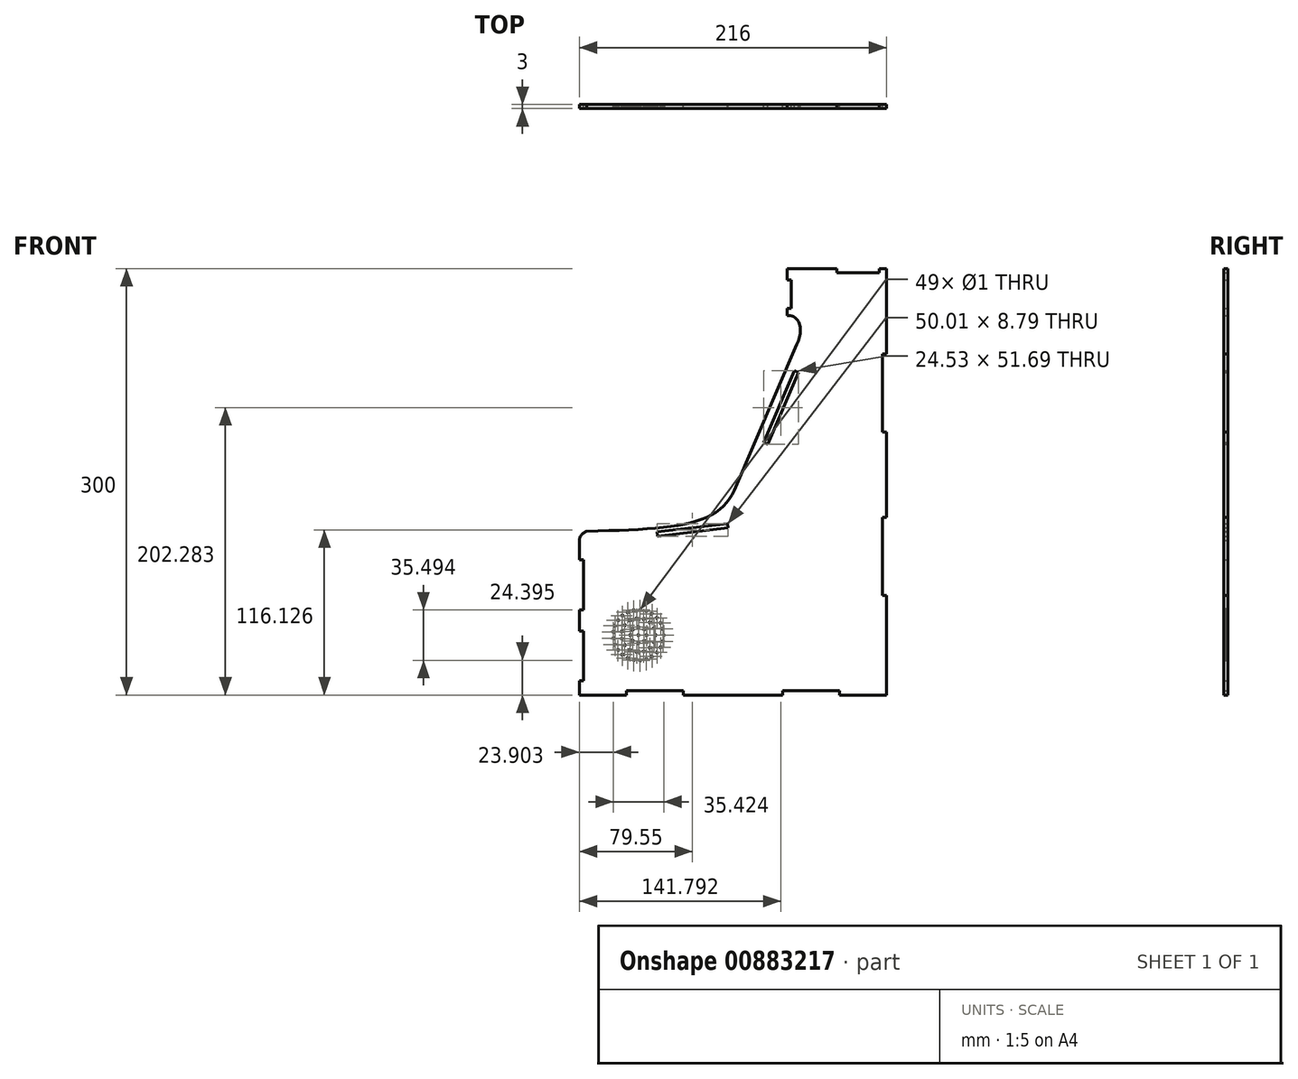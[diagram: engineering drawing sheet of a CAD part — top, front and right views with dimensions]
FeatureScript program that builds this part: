
annotation { "Feature Type Name" : "Feature", "Feature Type Description" : "" }
export const myFeature = defineFeature(function(context is Context, id is Id, definition is map)
    precondition{}
    {
        {
            var Q0;
            Q0=qCreatedBy(makeId("Front.planeOp"),FACE);
            var sketch = newSketch(context, id + "F0", { "sketchPlane" : qUnion([Q0])});
            skLineSegment(sketch, "E0.bottom", {"start": v(0, 0) * mm, "end": v(216, 0) * mm});
            skLineSegment(sketch, "E0.left", {"start": v(0, 0) * mm, "end": v(0, 115) * mm});
            skLineSegment(sketch, "E0.right", {"start": v(216, 0) * mm, "end": v(216, 300) * mm});
            skLineSegment(sketch, "E1", {"start": v(216, 300) * mm, "end": v(176, 300) * mm});
            skLineSegment(sketch, "E2", {"start": v(143, 0) * mm, "end": v(143, 3) * mm});
            skLineSegment(sketch, "E3", {"start": v(143, 3) * mm, "end": v(183, 3) * mm});
            skLineSegment(sketch, "E4", {"start": v(183, 3) * mm, "end": v(183, 0) * mm});
            skLineSegment(sketch, "E5", {"start": v(0, 45) * mm, "end": v(3, 45) * mm});
            skLineSegment(sketch, "E6", {"start": v(3, 45) * mm, "end": v(3, 10) * mm});
            skLineSegment(sketch, "E7", {"start": v(3, 10) * mm, "end": v(0, 10) * mm});
            skLineSegment(sketch, "E8", {"start": v(216, 125) * mm, "end": v(213, 125) * mm});
            skLineSegment(sketch, "E9", {"start": v(213, 125) * mm, "end": v(213, 70) * mm});
            skLineSegment(sketch, "E10", {"start": v(213, 70) * mm, "end": v(216, 70) * mm});
            skLineSegment(sketch, "E11", {"start": v(176, 300) * mm, "end": v(108.8, 144.17) * mm});
            skLineSegment(sketch, "E12", {"start": v(181, 300) * mm, "end": v(181, 297) * mm});
            skLineSegment(sketch, "E13", {"start": v(181, 297) * mm, "end": v(211, 297) * mm});
            skLineSegment(sketch, "E14", {"start": v(211, 297) * mm, "end": v(211, 300) * mm});
            skLineSegment(sketch, "E15", {"start": v(54.54, 114.7) * mm, "end": v(54.9, 111.73) * mm});
            skLineSegment(sketch, "E16", {"start": v(54.9, 111.73) * mm, "end": v(104.55, 117.54) * mm});
            skLineSegment(sketch, "E17", {"start": v(104.55, 117.54) * mm, "end": v(104.2, 120.52) * mm});
            skLineSegment(sketch, "E18", {"start": v(54.54, 114.7) * mm, "end": v(104.2, 120.52) * mm});
            skLineSegment(sketch, "E19", {"start": v(181, 297) * mm, "end": v(130.46, 179.8) * mm, "construction": true});
            skLineSegment(sketch, "E20", {"start": v(151.3, 228.13) * mm, "end": v(154.06, 226.94) * mm});
            skLineSegment(sketch, "E21", {"start": v(154.06, 226.94) * mm, "end": v(132.28, 176.44) * mm});
            skLineSegment(sketch, "E22", {"start": v(132.28, 176.44) * mm, "end": v(129.53, 177.62) * mm});
            skLineSegment(sketch, "E23", {"start": v(129.53, 177.62) * mm, "end": v(151.3, 228.13) * mm});
            skLineSegment(sketch, "E24", {"start": v(174.7, 297) * mm, "end": v(146, 297) * mm});
            skLineSegment(sketch, "E25", {"start": v(146, 297) * mm, "end": v(146, 267) * mm});
            skLineSegment(sketch, "E26", {"start": v(146, 267) * mm, "end": v(161.77, 267) * mm});
            skLineSegment(sketch, "E27", {"start": v(146, 292) * mm, "end": v(149, 292) * mm});
            skLineSegment(sketch, "E28", {"start": v(149, 292) * mm, "end": v(149, 272) * mm});
            skLineSegment(sketch, "E29", {"start": v(149, 272) * mm, "end": v(146, 272) * mm});
            skLineSegment(sketch, "E30", {"start": v(216, 240) * mm, "end": v(213, 240) * mm});
            skLineSegment(sketch, "E31", {"start": v(213, 240) * mm, "end": v(213, 185) * mm});
            skLineSegment(sketch, "E32", {"start": v(213, 185) * mm, "end": v(216, 185) * mm});
            skLineSegment(sketch, "E33", {"start": v(146, 297) * mm, "end": v(146, 300) * mm});
            skLineSegment(sketch, "E34", {"start": v(146, 300) * mm, "end": v(176, 300) * mm});
            skLineSegment(sketch, "E35", {"start": v(0, 95) * mm, "end": v(3, 95) * mm});
            skLineSegment(sketch, "E36", {"start": v(3, 95) * mm, "end": v(3, 60) * mm});
            skLineSegment(sketch, "E37", {"start": v(3, 60) * mm, "end": v(0, 60) * mm});
            skLineSegment(sketch, "E38", {"start": v(73, 0) * mm, "end": v(73, 3) * mm});
            skLineSegment(sketch, "E39", {"start": v(73, 3) * mm, "end": v(33, 3) * mm});
            skLineSegment(sketch, "E40", {"start": v(33, 3) * mm, "end": v(33, 0) * mm});
            skFitSpline(sketch, "E41", {"points": [v(146, 267) * mm, v(152.92, 246.47) * mm], "startDerivative": vector(30.33, 0) * mm, "endDerivative": vector(-13.3, -30.85) * mm});
            skFitSpline(sketch, "E42", {"points": [v(0, 115) * mm, v(108.8, 144.17) * mm], "startDerivative": vector(196.45, 5.74) * mm, "endDerivative": vector(34.04, 78.95) * mm});
            skArc(sketch, "E43", {"start": v(5.24, 115.15) * mm, "mid": v(1.25, 112.35) * mm, "end": v(0, 107.65) * mm});
            skLineSegment(sketch, "E44", {"start": v(5.24, 115.15) * mm, "end": v(195.42, 121.16) * mm, "construction": true});
            skSolve(sketch);
        }
        {
            var Q0;
            Q0=makeQuery(id+"F0.imprint","IMPRINT",FACE,{"disambiguationData":[TD([[makeQuery(id+"F0.imprint","IMPRINT",EDGE,{"derivedFrom":sQuery(id+"F0.wireOp",EDGE,"xnVY2FZi-heLS-hvb6-dwYe-Yhq741IxrDyy")}),1.0]])]});
            var Q1;
            {var subQ1=sQuery(id+"F0.wireOp",EDGE,"E0.left");Q1=makeQuery(id+"F0.imprint","IMPRINT",FACE,{"disambiguationData":[TD([[makeQuery(id+"F0.imprint","IMPRINT",EDGE,{"derivedFrom":subQ1}),-1.0]])]});}
            var Q2;
            {var subQ0=sQuery(id+"F0.wireOp",EDGE,"E24");Q2=makeQuery(id+"F0.imprint","IMPRINT",FACE,{"disambiguationData":[TD([[makeQuery(id+"F0.imprint","IMPRINT",EDGE,{"derivedFrom":subQ0}),1.0]])]});}
            var Q3;
            {var subQ2=sQuery(id+"F0.wireOp",EDGE,"E24");Q3=makeQuery(id+"F0.imprint","IMPRINT",FACE,{"disambiguationData":[TD([[makeQuery(id+"F0.imprint","IMPRINT",EDGE,{"derivedFrom":subQ2}),-1.0]])]});}
            var Q4;
            {var subQ0=sQuery(id+"F0.wireOp",EDGE,"RHPJXZOW-DbAP-qya6-Vzhz-GZjQZD372PIZ");Q4=makeQuery(id+"F0.imprint","IMPRINT",FACE,{"disambiguationData":[TD([[makeQuery(id+"F0.imprint","IMPRINT",EDGE,{"derivedFrom":subQ0}),-1.0]])]});}
            var Q5;
            {var subQ0=sQuery(id+"F0.wireOp",EDGE,"E26");Q5=makeQuery(id+"F0.imprint","IMPRINT",FACE,{"disambiguationData":[TD([[makeQuery(id+"F0.imprint","IMPRINT",EDGE,{"derivedFrom":subQ0}),-1.0]])]});}
            extrude(context, id + "F1", {"entities" : qUnion([Q0, Q1, Q2, Q3, Q4, Q5]), "depth" : 3 * mm, "offsetDistance" : 25 * mm});
        }
        {
            var Q0;
            Q0=makeQuery(id+"F1.opExtrude","CAP_FACE",FACE,{"disambiguationData":[OSD([sQuery(id+"F0.wireOp",EDGE,"E0.bottom"),sQuery(id+"F0.wireOp",EDGE,"E0.left"),sQuery(id+"F0.wireOp",EDGE,"E0.right"),sQuery(id+"F0.wireOp",EDGE,"E1"),sQuery(id+"F0.wireOp",EDGE,"E2"),sQuery(id+"F0.wireOp",EDGE,"E3"),sQuery(id+"F0.wireOp",EDGE,"E4"),sQuery(id+"F0.wireOp",EDGE,"E5"),sQuery(id+"F0.wireOp",EDGE,"E6"),sQuery(id+"F0.wireOp",EDGE,"E7"),sQuery(id+"F0.wireOp",EDGE,"E8"),sQuery(id+"F0.wireOp",EDGE,"E9"),sQuery(id+"F0.wireOp",EDGE,"E10"),sQuery(id+"F0.wireOp",EDGE,"E11"),sQuery(id+"F0.wireOp",EDGE,"RHPJXZOW-DbAP-qya6-Vzhz-GZjQZD372PIZ"),sQuery(id+"F0.wireOp",EDGE,"E12"),sQuery(id+"F0.wireOp",EDGE,"E13"),sQuery(id+"F0.wireOp",EDGE,"E14"),sQuery(id+"F0.wireOp",EDGE,"E15"),sQuery(id+"F0.wireOp",EDGE,"E16"),sQuery(id+"F0.wireOp",EDGE,"E17"),sQuery(id+"F0.wireOp",EDGE,"E18"),sQuery(id+"F0.wireOp",EDGE,"E20"),sQuery(id+"F0.wireOp",EDGE,"E21"),sQuery(id+"F0.wireOp",EDGE,"E22"),sQuery(id+"F0.wireOp",EDGE,"E23")])],"isStart":false});
            var sketch = newSketch(context, id + "F2", { "sketchPlane" : qUnion([Q0])});
            skCircle(sketch, "E45", {"center": v(41.54, 42.14) * mm, "radius": 0.5 * mm});
            skCircle(sketch, "E46", {"center": v(47.23, 42.14) * mm, "radius": 0.5 * mm});
            skCircle(sketch, "E47", {"center": v(53.48, 42.14) * mm, "radius": 0.5 * mm});
            skCircle(sketch, "E48", {"center": v(59.33, 42.14) * mm, "radius": 0.5 * mm});
            skCircle(sketch, "E49.1.0", {"center": v(45.56, 46.16) * mm, "radius": 0.5 * mm});
            skCircle(sketch, "E49.2.0", {"center": v(41.54, 47.83) * mm, "radius": 0.5 * mm});
            skCircle(sketch, "E49.3.0", {"center": v(37.53, 46.16) * mm, "radius": 0.5 * mm});
            skCircle(sketch, "E49.4.0", {"center": v(35.86, 42.14) * mm, "radius": 0.5 * mm});
            skCircle(sketch, "E49.5.0", {"center": v(37.53, 38.12) * mm, "radius": 0.5 * mm});
            skCircle(sketch, "E49.6.0", {"center": v(41.54, 36.46) * mm, "radius": 0.5 * mm});
            skCircle(sketch, "E49.7.0", {"center": v(45.56, 38.12) * mm, "radius": 0.5 * mm});
            skCircle(sketch, "E50.1.0", {"center": v(52.45, 47) * mm, "radius": 0.5 * mm});
            skCircle(sketch, "E50.2.0", {"center": v(49.53, 51.01) * mm, "radius": 0.5 * mm});
            skCircle(sketch, "E50.3.0", {"center": v(45.23, 53.5) * mm, "radius": 0.5 * mm});
            skCircle(sketch, "E50.4.0", {"center": v(40.3, 54.02) * mm, "radius": 0.5 * mm});
            skCircle(sketch, "E50.5.0", {"center": v(35.57, 52.48) * mm, "radius": 0.5 * mm});
            skCircle(sketch, "E50.6.0", {"center": v(31.89, 49.16) * mm, "radius": 0.5 * mm});
            skCircle(sketch, "E50.7.0", {"center": v(29.87, 44.62) * mm, "radius": 0.5 * mm});
            skCircle(sketch, "E50.8.0", {"center": v(29.87, 39.66) * mm, "radius": 0.5 * mm});
            skCircle(sketch, "E50.9.0", {"center": v(31.89, 35.12) * mm, "radius": 0.5 * mm});
            skCircle(sketch, "E50.10.0", {"center": v(35.57, 31.8) * mm, "radius": 0.5 * mm});
            skCircle(sketch, "E50.11.0", {"center": v(40.3, 30.27) * mm, "radius": 0.5 * mm});
            skCircle(sketch, "E50.12.0", {"center": v(45.23, 30.79) * mm, "radius": 0.5 * mm});
            skCircle(sketch, "E50.13.0", {"center": v(49.53, 33.27) * mm, "radius": 0.5 * mm});
            skCircle(sketch, "E50.14.0", {"center": v(52.45, 37.29) * mm, "radius": 0.5 * mm});
            skCircle(sketch, "E51.1.0", {"center": v(58.77, 46.56) * mm, "radius": 0.5 * mm});
            skCircle(sketch, "E51.2.0", {"center": v(57.13, 50.7) * mm, "radius": 0.5 * mm});
            skCircle(sketch, "E51.3.0", {"center": v(54.5, 54.31) * mm, "radius": 0.5 * mm});
            skCircle(sketch, "E51.4.0", {"center": v(51.07, 57.16) * mm, "radius": 0.5 * mm});
            skCircle(sketch, "E51.5.0", {"center": v(47.04, 59.05) * mm, "radius": 0.5 * mm});
            skCircle(sketch, "E51.6.0", {"center": v(42.66, 59.89) * mm, "radius": 0.5 * mm});
            skCircle(sketch, "E51.7.0", {"center": v(38.21, 59.6) * mm, "radius": 0.5 * mm});
            skCircle(sketch, "E51.8.0", {"center": v(33.97, 58.23) * mm, "radius": 0.5 * mm});
            skCircle(sketch, "E51.9.0", {"center": v(30.2, 55.84) * mm, "radius": 0.5 * mm});
            skCircle(sketch, "E51.10.0", {"center": v(27.16, 52.6) * mm, "radius": 0.5 * mm});
            skCircle(sketch, "E51.11.0", {"center": v(25.01, 48.69) * mm, "radius": 0.5 * mm});
            skCircle(sketch, "E51.12.0", {"center": v(23.9, 44.37) * mm, "radius": 0.5 * mm});
            skCircle(sketch, "E51.13.0", {"center": v(23.9, 39.91) * mm, "radius": 0.5 * mm});
            skCircle(sketch, "E51.14.0", {"center": v(25.01, 35.6) * mm, "radius": 0.5 * mm});
            skCircle(sketch, "E51.15.0", {"center": v(27.16, 31.7) * mm, "radius": 0.5 * mm});
            skCircle(sketch, "E51.16.0", {"center": v(30.2, 28.44) * mm, "radius": 0.5 * mm});
            skCircle(sketch, "E51.17.0", {"center": v(33.97, 26.05) * mm, "radius": 0.5 * mm});
            skCircle(sketch, "E51.18.0", {"center": v(38.21, 24.68) * mm, "radius": 0.5 * mm});
            skCircle(sketch, "E51.19.0", {"center": v(42.66, 24.4) * mm, "radius": 0.5 * mm});
            skCircle(sketch, "E51.20.0", {"center": v(47.04, 25.23) * mm, "radius": 0.5 * mm});
            skCircle(sketch, "E51.21.0", {"center": v(51.07, 27.13) * mm, "radius": 0.5 * mm});
            skCircle(sketch, "E51.22.0", {"center": v(54.5, 29.97) * mm, "radius": 0.5 * mm});
            skCircle(sketch, "E51.23.0", {"center": v(57.13, 33.58) * mm, "radius": 0.5 * mm});
            skCircle(sketch, "E51.24.0", {"center": v(58.77, 37.72) * mm, "radius": 0.5 * mm});
            skSolve(sketch);
        }
        {
            var Q0;
            Q0 = qSketchRegion(id + "F2", true);
            extrude(context, id + "F3", {"entities" : qUnion([Q0]), "operationType" : NewBodyOperationType.REMOVE, "endBound" : BoundingType.UP_TO_NEXT, "oppositeDirection" : true, "depth" : 25 * mm, "offsetDistance" : 25 * mm});
        }
    });
